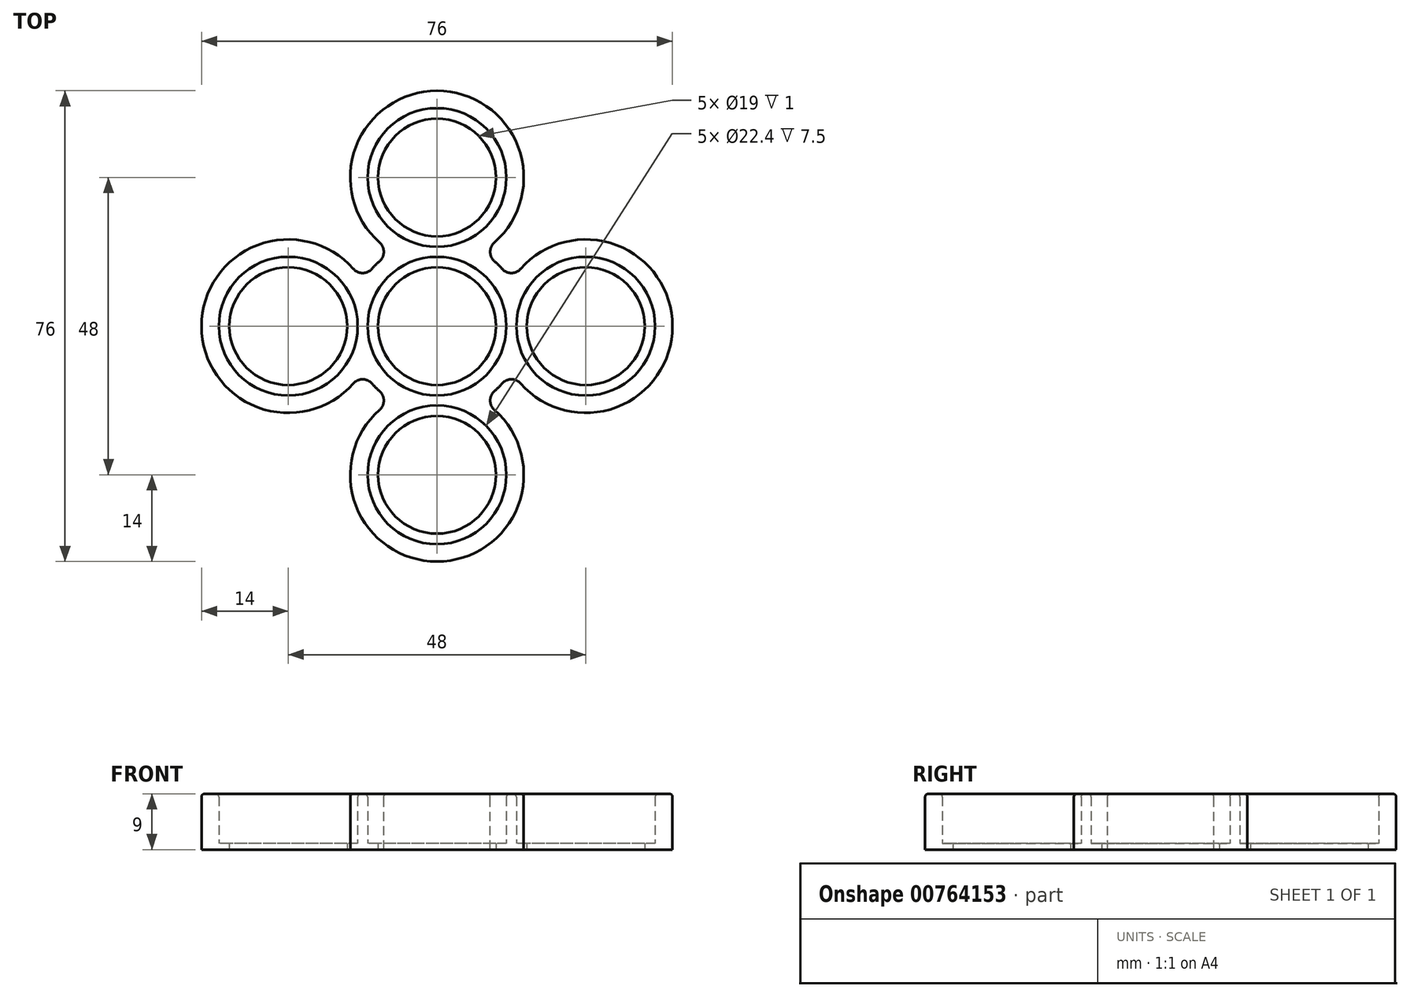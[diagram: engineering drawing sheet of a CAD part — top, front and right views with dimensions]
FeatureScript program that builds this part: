
annotation { "Feature Type Name" : "Feature", "Feature Type Description" : "" }
export const myFeature = defineFeature(function(context is Context, id is Id, definition is map)
    precondition{}
    {
        {
            var Q0;
            Q0=qCreatedBy(makeId("Top.planeOp"),FACE);
            var sketch = newSketch(context, id + "F0", { "sketchPlane" : qUnion([Q0])});
            skCircle(sketch, "E0", {"center": v(0, 0) * mm, "radius": 11.2 * mm});
            skCircle(sketch, "E1", {"center": v(0, 0) * mm, "radius": 14 * mm});
            skCircle(sketch, "E2", {"center": v(0, 24) * mm, "radius": 11.2 * mm});
            skCircle(sketch, "E3", {"center": v(0, 24) * mm, "radius": 14 * mm});
            skLineSegment(sketch, "E4", {"start": v(0, 24) * mm, "end": v(0, 0) * mm, "construction": true});
            skLineSegment(sketch, "E5", {"start": v(0, 0) * mm, "end": v(24, 0) * mm, "construction": true});
            skCircle(sketch, "E6", {"center": v(24, 0) * mm, "radius": 11.2 * mm});
            skCircle(sketch, "E7", {"center": v(24, 0) * mm, "radius": 14 * mm});
            skLineSegment(sketch, "E8", {"start": v(0, 0) * mm, "end": v(-24, 0) * mm, "construction": true});
            skCircle(sketch, "E9", {"center": v(-24, 0) * mm, "radius": 11.2 * mm});
            skCircle(sketch, "E10", {"center": v(-24, 0) * mm, "radius": 14 * mm});
            skCircle(sketch, "E11", {"center": v(0, 24) * mm, "radius": 9.5 * mm});
            skCircle(sketch, "E12", {"center": v(-24, 0) * mm, "radius": 9.5 * mm});
            skCircle(sketch, "E13", {"center": v(24, 0) * mm, "radius": 9.5 * mm});
            skCircle(sketch, "E14", {"center": v(0, 0) * mm, "radius": 9.5 * mm});
            skCircle(sketch, "E15", {"center": v(0, -24) * mm, "radius": 9.5 * mm});
            skCircle(sketch, "E16", {"center": v(0, -24) * mm, "radius": 11.2 * mm});
            skCircle(sketch, "E17", {"center": v(0, -24) * mm, "radius": 14 * mm});
            skLineSegment(sketch, "E18", {"start": v(0, -24) * mm, "end": v(0, 0) * mm, "construction": true});
            skSolve(sketch);
        }
        {
            var Q0;
            Q0=qSketchRegion(id+"F0",true);
            var Q1;
            Q1=makeQuery(id+"F0.imprint","IMPRINT",FACE,{"disambiguationData":[TD([[makeQuery(id+"F0.imprint","IMPRINT",EDGE,{"derivedFrom":sQuery(id+"F0.wireOp",EDGE,"E0")}),1.0]])]});
            var Q2;
            {var subQ0=sQuery(id+"F0.wireOp",EDGE,"E2");var subQ1=sQuery(id+"F0.wireOp",EDGE,"E1");var subQ2=makeQuery(id+"F0.imprint","INTERSECT",VERTEX,{"disambiguationData":[OD(0.0)],"derivedFrom":[subQ1,subQ0]});Q2=makeQuery(id+"F0.imprint","IMPRINT",FACE,{"disambiguationData":[TD([[makeQuery(id+"F0.imprint","IMPRINT",EDGE,{"disambiguationData":[TD([[subQ2,-1.0]])],"derivedFrom":subQ1}),1.0]])]});}
            var Q3;
            {var subQ0=sQuery(id+"F0.wireOp",EDGE,"E2");var subQ1=sQuery(id+"F0.wireOp",EDGE,"E1");var subQ2=makeQuery(id+"F0.imprint","INTERSECT",VERTEX,{"disambiguationData":[OD(0.0)],"derivedFrom":[subQ1,subQ0]});Q3=makeQuery(id+"F0.imprint","IMPRINT",FACE,{"disambiguationData":[TD([[makeQuery(id+"F0.imprint","IMPRINT",EDGE,{"disambiguationData":[TD([[subQ2,-1.0]])],"derivedFrom":subQ1}),-1.0]])]});}
            var Q4;
            {var subQ0=sQuery(id+"F0.wireOp",EDGE,"E9");var subQ1=sQuery(id+"F0.wireOp",EDGE,"E1");var subQ2=makeQuery(id+"F0.imprint","INTERSECT",VERTEX,{"disambiguationData":[OD(0.0)],"derivedFrom":[subQ1,subQ0]});Q4=makeQuery(id+"F0.imprint","IMPRINT",FACE,{"disambiguationData":[TD([[makeQuery(id+"F0.imprint","IMPRINT",EDGE,{"disambiguationData":[TD([[subQ2,-1.0]])],"derivedFrom":subQ1}),1.0]])]});}
            var Q5;
            {var subQ0=sQuery(id+"F0.wireOp",EDGE,"E9");var subQ1=sQuery(id+"F0.wireOp",EDGE,"E1");var subQ2=makeQuery(id+"F0.imprint","INTERSECT",VERTEX,{"disambiguationData":[OD(0.0)],"derivedFrom":[subQ1,subQ0]});Q5=makeQuery(id+"F0.imprint","IMPRINT",FACE,{"disambiguationData":[TD([[makeQuery(id+"F0.imprint","IMPRINT",EDGE,{"disambiguationData":[TD([[subQ2,-1.0]])],"derivedFrom":subQ1}),-1.0]])]});}
            var Q6;
            {var subQ0=sQuery(id+"F0.wireOp",EDGE,"E6");var subQ1=sQuery(id+"F0.wireOp",EDGE,"E1");var subQ2=makeQuery(id+"F0.imprint","INTERSECT",VERTEX,{"disambiguationData":[OD(0.0)],"derivedFrom":[subQ1,subQ0]});Q6=makeQuery(id+"F0.imprint","IMPRINT",FACE,{"disambiguationData":[TD([[makeQuery(id+"F0.imprint","IMPRINT",EDGE,{"disambiguationData":[TD([[subQ2,-1.0]])],"derivedFrom":subQ1}),1.0]])]});}
            var Q7;
            {var subQ0=sQuery(id+"F0.wireOp",EDGE,"E6");var subQ1=sQuery(id+"F0.wireOp",EDGE,"E1");var subQ2=makeQuery(id+"F0.imprint","INTERSECT",VERTEX,{"disambiguationData":[OD(0.0)],"derivedFrom":[subQ1,subQ0]});Q7=makeQuery(id+"F0.imprint","IMPRINT",FACE,{"disambiguationData":[TD([[makeQuery(id+"F0.imprint","IMPRINT",EDGE,{"disambiguationData":[TD([[subQ2,-1.0]])],"derivedFrom":subQ1}),-1.0]])]});}
            var Q8;
            {var subQ0=sQuery(id+"F0.wireOp",EDGE,"E10");var subQ1=sQuery(id+"F0.wireOp",EDGE,"E0");var subQ2=makeQuery(id+"F0.imprint","INTERSECT",VERTEX,{"disambiguationData":[OD(0.0)],"derivedFrom":[subQ1,subQ0]});Q8=makeQuery(id+"F0.imprint","IMPRINT",FACE,{"disambiguationData":[TD([[makeQuery(id+"F0.imprint","IMPRINT",EDGE,{"disambiguationData":[TD([[subQ2,-1.0]])],"derivedFrom":subQ1}),1.0]])]});}
            var Q9;
            {var subQ0=sQuery(id+"F0.wireOp",EDGE,"E7");var subQ1=sQuery(id+"F0.wireOp",EDGE,"E0");var subQ2=makeQuery(id+"F0.imprint","INTERSECT",VERTEX,{"disambiguationData":[OD(0.0)],"derivedFrom":[subQ1,subQ0]});Q9=makeQuery(id+"F0.imprint","IMPRINT",FACE,{"disambiguationData":[TD([[makeQuery(id+"F0.imprint","IMPRINT",EDGE,{"disambiguationData":[TD([[subQ2,-1.0]])],"derivedFrom":subQ1}),1.0]])]});}
            var Q10;
            {var subQ0=sQuery(id+"F0.wireOp",EDGE,"E3");var subQ1=sQuery(id+"F0.wireOp",EDGE,"E0");var subQ2=makeQuery(id+"F0.imprint","INTERSECT",VERTEX,{"disambiguationData":[OD(0.0)],"derivedFrom":[subQ1,subQ0]});Q10=makeQuery(id+"F0.imprint","IMPRINT",FACE,{"disambiguationData":[TD([[makeQuery(id+"F0.imprint","IMPRINT",EDGE,{"disambiguationData":[TD([[subQ2,1.0]])],"derivedFrom":subQ1}),1.0]])]});}
            var Q11;
            {var subQ0=sQuery(id+"F0.wireOp",EDGE,"E17");var subQ1=sQuery(id+"F0.wireOp",EDGE,"E0");var subQ2=makeQuery(id+"F0.imprint","INTERSECT",VERTEX,{"disambiguationData":[OD(0.0)],"derivedFrom":[subQ1,subQ0]});Q11=makeQuery(id+"F0.imprint","IMPRINT",FACE,{"disambiguationData":[TD([[makeQuery(id+"F0.imprint","IMPRINT",EDGE,{"disambiguationData":[TD([[subQ2,-1.0]])],"derivedFrom":subQ1}),1.0]])]});}
            var Q12;
            {var subQ0=sQuery(id+"F0.wireOp",EDGE,"E7");var subQ1=sQuery(id+"F0.wireOp",EDGE,"E0");var subQ2=makeQuery(id+"F0.imprint","INTERSECT",VERTEX,{"disambiguationData":[OD(0.0)],"derivedFrom":[subQ1,subQ0]});Q12=makeQuery(id+"F0.imprint","IMPRINT",FACE,{"disambiguationData":[TD([[makeQuery(id+"F0.imprint","IMPRINT",EDGE,{"disambiguationData":[TD([[subQ2,1.0]])],"derivedFrom":subQ1}),1.0]])]});}
            var Q13;
            {var subQ0=sQuery(id+"F0.wireOp",EDGE,"E3");var subQ1=sQuery(id+"F0.wireOp",EDGE,"E0");var subQ2=makeQuery(id+"F0.imprint","INTERSECT",VERTEX,{"disambiguationData":[OD(0.0)],"derivedFrom":[subQ1,subQ0]});Q13=makeQuery(id+"F0.imprint","IMPRINT",FACE,{"disambiguationData":[TD([[makeQuery(id+"F0.imprint","IMPRINT",EDGE,{"disambiguationData":[TD([[subQ2,-1.0]])],"derivedFrom":subQ1}),1.0]])]});}
            var Q14;
            Q14=makeQuery(id+"F0.imprint","IMPRINT",FACE,{"disambiguationData":[TD([[makeQuery(id+"F0.imprint","IMPRINT",EDGE,{"derivedFrom":sQuery(id+"F0.wireOp",EDGE,"E15")}),-1.0]])]});
            var Q15;
            Q15=makeQuery(id+"F0.imprint","IMPRINT",FACE,{"disambiguationData":[TD([[makeQuery(id+"F0.imprint","IMPRINT",EDGE,{"derivedFrom":sQuery(id+"F0.wireOp",EDGE,"E13")}),-1.0]])]});
            var Q16;
            {var subQ0=sQuery(id+"F0.wireOp",EDGE,"E16");var subQ1=sQuery(id+"F0.wireOp",EDGE,"E1");var subQ2=makeQuery(id+"F0.imprint","INTERSECT",VERTEX,{"disambiguationData":[OD(0.0)],"derivedFrom":[subQ1,subQ0]});Q16=makeQuery(id+"F0.imprint","IMPRINT",FACE,{"disambiguationData":[TD([[makeQuery(id+"F0.imprint","IMPRINT",EDGE,{"disambiguationData":[TD([[subQ2,-1.0]])],"derivedFrom":subQ1}),1.0]])]});}
            var Q17;
            {var subQ0=sQuery(id+"F0.wireOp",EDGE,"E6");var subQ1=sQuery(id+"F0.wireOp",EDGE,"E1");var subQ2=makeQuery(id+"F0.imprint","INTERSECT",VERTEX,{"disambiguationData":[OD(0.0)],"derivedFrom":[subQ1,subQ0]});Q17=makeQuery(id+"F0.imprint","IMPRINT",FACE,{"disambiguationData":[TD([[makeQuery(id+"F0.imprint","IMPRINT",EDGE,{"disambiguationData":[TD([[subQ2,1.0]])],"derivedFrom":subQ1}),1.0]])]});}
            extrude(context, id + "F1", {"entities" : qUnion([Q0, Q1, Q2, Q3, Q4, Q5, Q6, Q7, Q8, Q9, Q10, Q11, Q12, Q13, Q14, Q15, Q16, Q17]), "depth" : 1 * mm, "offsetDistance" : 25 * mm});
        }
        {
            var Q0;
            Q0=qSketchRegion(id+"F0",true);
            extrude(context, id + "F2", {"entities" : qUnion([Q0]), "operationType" : NewBodyOperationType.ADD, "depth" : 9 * mm, "offsetDistance" : 25 * mm});
        }
        {
            var Q0;
            {var subQ0=sQuery(id+"F0.wireOp",EDGE,"E3");var subQ1=sQuery(id+"F0.wireOp",EDGE,"E1");var subQ2=makeQuery(id+"F0.imprint","INTERSECT",VERTEX,{"disambiguationData":[OD(1.0)],"derivedFrom":[subQ1,subQ0]});Q0=makeQuery(id+"F2.boolean.opBoolean","MERGE",EDGE,{"derivedFrom":[makeQuery(id+"F1.opExtrude","SWEPT_EDGE",EDGE,{"disambiguationData":[OSD([subQ1,subQ0]),TDD([subQ2])]}),makeQuery(id+"F2.opExtrude","SWEPT_EDGE",EDGE,{"disambiguationData":[OSD([subQ1,subQ0]),TDD([subQ2])]})]});}
            var Q1;
            {var subQ0=sQuery(id+"F0.wireOp",EDGE,"E10");var subQ1=sQuery(id+"F0.wireOp",EDGE,"E1");var subQ2=makeQuery(id+"F0.imprint","INTERSECT",VERTEX,{"disambiguationData":[OD(0.0)],"derivedFrom":[subQ1,subQ0]});Q1=makeQuery(id+"F2.boolean.opBoolean","MERGE",EDGE,{"derivedFrom":[makeQuery(id+"F1.opExtrude","SWEPT_EDGE",EDGE,{"disambiguationData":[OSD([subQ1,subQ0]),TDD([subQ2])]}),makeQuery(id+"F2.opExtrude","SWEPT_EDGE",EDGE,{"disambiguationData":[OSD([subQ1,subQ0]),TDD([subQ2])]})]});}
            var Q2;
            {var subQ0=sQuery(id+"F0.wireOp",EDGE,"E10");var subQ1=sQuery(id+"F0.wireOp",EDGE,"E1");var subQ2=makeQuery(id+"F0.imprint","INTERSECT",VERTEX,{"disambiguationData":[OD(1.0)],"derivedFrom":[subQ1,subQ0]});Q2=makeQuery(id+"F2.boolean.opBoolean","MERGE",EDGE,{"derivedFrom":[makeQuery(id+"F1.opExtrude","SWEPT_EDGE",EDGE,{"disambiguationData":[OSD([subQ1,subQ0]),TDD([subQ2])]}),makeQuery(id+"F2.opExtrude","SWEPT_EDGE",EDGE,{"disambiguationData":[OSD([subQ1,subQ0]),TDD([subQ2])]})]});}
            var Q3;
            {var subQ0=sQuery(id+"F0.wireOp",EDGE,"E7");var subQ1=sQuery(id+"F0.wireOp",EDGE,"E1");var subQ2=makeQuery(id+"F0.imprint","INTERSECT",VERTEX,{"disambiguationData":[OD(1.0)],"derivedFrom":[subQ1,subQ0]});Q3=makeQuery(id+"F2.boolean.opBoolean","MERGE",EDGE,{"derivedFrom":[makeQuery(id+"F1.opExtrude","SWEPT_EDGE",EDGE,{"disambiguationData":[OSD([subQ1,subQ0]),TDD([subQ2])]}),makeQuery(id+"F2.opExtrude","SWEPT_EDGE",EDGE,{"disambiguationData":[OSD([subQ1,subQ0]),TDD([subQ2])]})]});}
            var Q4;
            {var subQ0=sQuery(id+"F0.wireOp",EDGE,"E7");var subQ1=sQuery(id+"F0.wireOp",EDGE,"E1");var subQ2=makeQuery(id+"F0.imprint","INTERSECT",VERTEX,{"disambiguationData":[OD(0.0)],"derivedFrom":[subQ1,subQ0]});Q4=makeQuery(id+"F2.boolean.opBoolean","MERGE",EDGE,{"derivedFrom":[makeQuery(id+"F1.opExtrude","SWEPT_EDGE",EDGE,{"disambiguationData":[OSD([subQ1,subQ0]),TDD([subQ2])]}),makeQuery(id+"F2.opExtrude","SWEPT_EDGE",EDGE,{"disambiguationData":[OSD([subQ1,subQ0]),TDD([subQ2])]})]});}
            var Q5;
            {var subQ0=sQuery(id+"F0.wireOp",EDGE,"E3");var subQ1=sQuery(id+"F0.wireOp",EDGE,"E1");var subQ2=makeQuery(id+"F0.imprint","INTERSECT",VERTEX,{"disambiguationData":[OD(0.0)],"derivedFrom":[subQ1,subQ0]});Q5=makeQuery(id+"F2.boolean.opBoolean","MERGE",EDGE,{"derivedFrom":[makeQuery(id+"F1.opExtrude","SWEPT_EDGE",EDGE,{"disambiguationData":[OSD([subQ1,subQ0]),TDD([subQ2])]}),makeQuery(id+"F2.opExtrude","SWEPT_EDGE",EDGE,{"disambiguationData":[OSD([subQ1,subQ0]),TDD([subQ2])]})]});}
            var Q6;
            {var subQ0=sQuery(id+"F0.wireOp",EDGE,"E17");var subQ1=sQuery(id+"F0.wireOp",EDGE,"E1");var subQ2=makeQuery(id+"F0.imprint","INTERSECT",VERTEX,{"disambiguationData":[OD(0.0)],"derivedFrom":[subQ1,subQ0]});Q6=makeQuery(id+"F2.boolean.opBoolean","MERGE",EDGE,{"derivedFrom":[makeQuery(id+"F1.opExtrude","SWEPT_EDGE",EDGE,{"disambiguationData":[OSD([subQ1,subQ0]),TDD([subQ2])]}),makeQuery(id+"F2.opExtrude","SWEPT_EDGE",EDGE,{"disambiguationData":[OSD([subQ1,subQ0]),TDD([subQ2])]})]});}
            var Q7;
            {var subQ0=sQuery(id+"F0.wireOp",EDGE,"E17");var subQ1=sQuery(id+"F0.wireOp",EDGE,"E1");var subQ2=makeQuery(id+"F0.imprint","INTERSECT",VERTEX,{"disambiguationData":[OD(1.0)],"derivedFrom":[subQ1,subQ0]});Q7=makeQuery(id+"F2.boolean.opBoolean","MERGE",EDGE,{"derivedFrom":[makeQuery(id+"F1.opExtrude","SWEPT_EDGE",EDGE,{"disambiguationData":[OSD([subQ1,subQ0]),TDD([subQ2])]}),makeQuery(id+"F2.opExtrude","SWEPT_EDGE",EDGE,{"disambiguationData":[OSD([subQ1,subQ0]),TDD([subQ2])]})]});}
            fillet(context, id + "F3", {"entities" : qUnion([Q0, Q1, Q2, Q3, Q4, Q5, Q6, Q7]), "radius" : 2 * mm, "tangentPropagation" : true, "allowEdgeOverflow" : false});
        }
        {
            var Q0;
            Q0=makeQuery(id+"F2.opExtrude","CAP_EDGE",EDGE,{"disambiguationData":[OSD([sQuery(id+"F0.wireOp",EDGE,"E3")])],"isStart":false});
            var Q1;
            Q1=makeQuery(id+"F2.opExtrude","CAP_EDGE",EDGE,{"disambiguationData":[OSD([sQuery(id+"F0.wireOp",EDGE,"E2")])],"isStart":false});
            var Q2;
            Q2=makeQuery(id+"F2.opExtrude","CAP_EDGE",EDGE,{"disambiguationData":[OSD([sQuery(id+"F0.wireOp",EDGE,"E9")])],"isStart":false});
            var Q3;
            Q3=makeQuery(id+"F2.opExtrude","CAP_EDGE",EDGE,{"disambiguationData":[OSD([sQuery(id+"F0.wireOp",EDGE,"E0")])],"isStart":false});
            var Q4;
            Q4=makeQuery(id+"F2.opExtrude","CAP_EDGE",EDGE,{"disambiguationData":[OSD([sQuery(id+"F0.wireOp",EDGE,"E6")])],"isStart":false});
            var Q5;
            Q5=makeQuery(id+"F2.opExtrude","CAP_EDGE",EDGE,{"disambiguationData":[OSD([sQuery(id+"F0.wireOp",EDGE,"E16")])],"isStart":false});
            fillet(context, id + "F4", {"entities" : qUnion([Q0, Q1, Q2, Q3, Q4, Q5]), "radius" : .5 * mm, "tangentPropagation" : true, "allowEdgeOverflow" : false});
        }
    });
